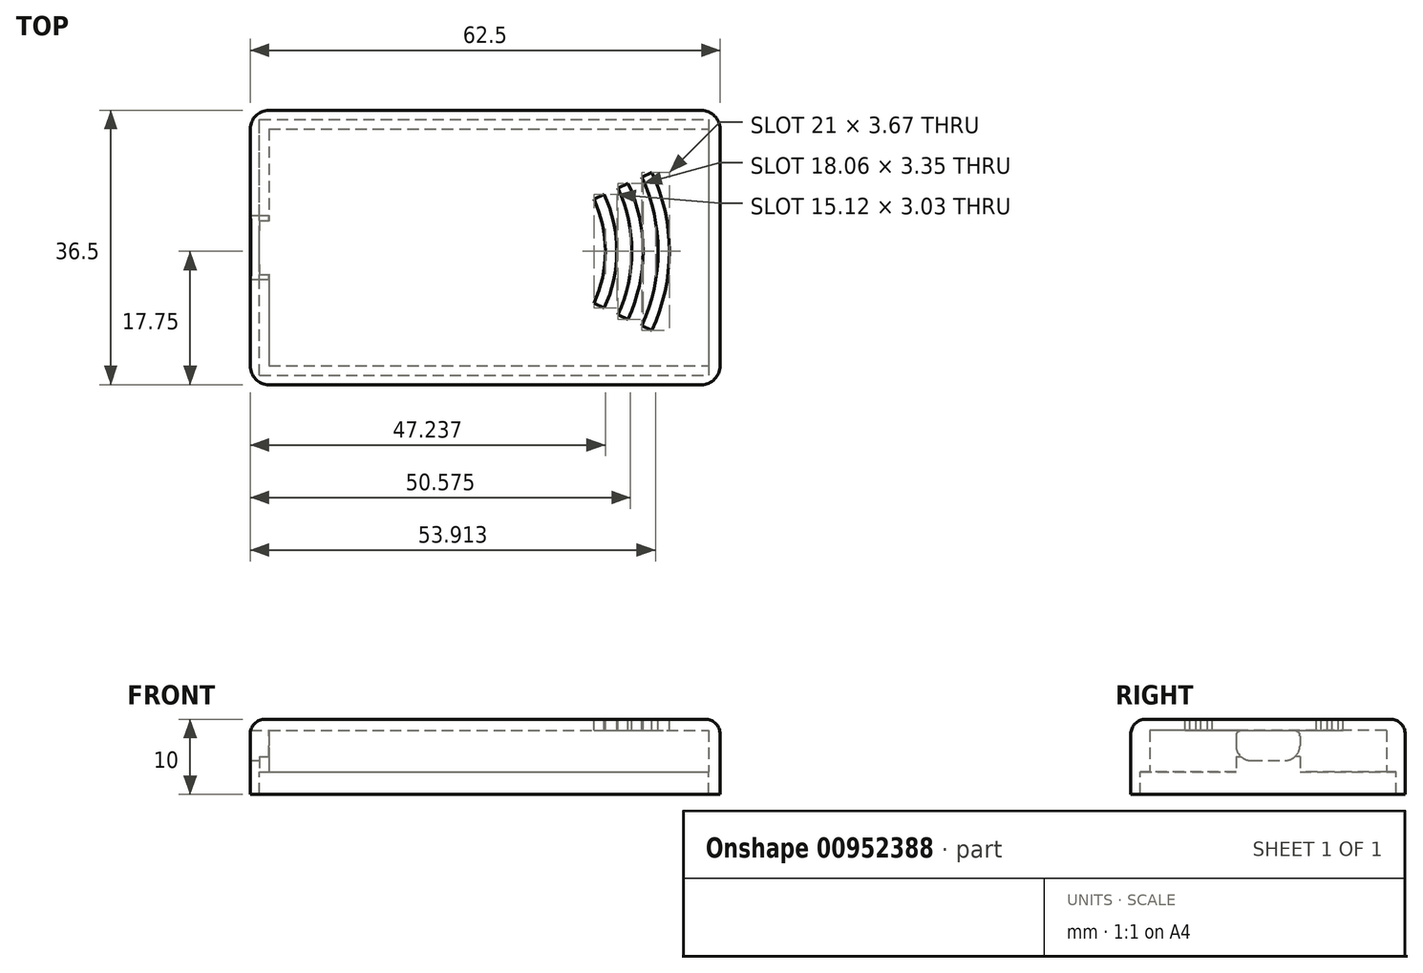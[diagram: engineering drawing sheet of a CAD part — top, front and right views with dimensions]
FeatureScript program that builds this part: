
annotation { "Feature Type Name" : "Feature", "Feature Type Description" : "" }
export const myFeature = defineFeature(function(context is Context, id is Id, definition is map)
    precondition{}
    {
        {
            var Q0;
            Q0=qCreatedBy(makeId("Top.planeOp"),FACE);
            var sketch = newSketch(context, id + "F0", { "sketchPlane" : qUnion([Q0])});
            skLineSegment(sketch, "E0.bottom", {"start": v(-30.75, 18.75) * mm, "end": v(31.75, 18.75) * mm});
            skLineSegment(sketch, "E0.top", {"start": v(-30.75, -17.75) * mm, "end": v(31.75, -17.75) * mm});
            skLineSegment(sketch, "E0.left", {"start": v(-30.75, 18.75) * mm, "end": v(-30.75, -17.75) * mm});
            skLineSegment(sketch, "E0.right", {"start": v(31.75, 18.75) * mm, "end": v(31.75, -17.75) * mm});
            skLineSegment(sketch, "E1.bottom", {"start": v(-28.25, 16.25) * mm, "end": v(30.25, 16.25) * mm});
            skLineSegment(sketch, "E1.top", {"start": v(-28.25, -15.25) * mm, "end": v(30.25, -15.25) * mm});
            skLineSegment(sketch, "E1.left", {"start": v(-28.25, 16.25) * mm, "end": v(-28.25, -15.25) * mm});
            skLineSegment(sketch, "E1.right", {"start": v(30.25, 16.25) * mm, "end": v(30.25, -15.25) * mm});
            skSolve(sketch);
        }
        {
            var Q0;
            Q0=makeQuery(id+"F0.imprint","IMPRINT",FACE,{"disambiguationData":[TD([[makeQuery(id+"F0.imprint","IMPRINT",EDGE,{"derivedFrom":sQuery(id+"F0.wireOp",EDGE,"E0.bottom")}),-1.0]])]});
            extrude(context, id + "F1", {"entities" : qUnion([Q0]), "offsetDistance" : 25 * mm, "depth" : 7 * mm});
        }
        {
            var Q0;
            Q0=makeQuery(id+"F1.opExtrude","CAP_FACE",FACE,{"disambiguationData":[OSD([sQuery(id+"F0.wireOp",EDGE,"E0.bottom"),sQuery(id+"F0.wireOp",EDGE,"E0.top"),sQuery(id+"F0.wireOp",EDGE,"E0.left"),sQuery(id+"F0.wireOp",EDGE,"E0.right"),sQuery(id+"F0.wireOp",EDGE,"E1.bottom"),sQuery(id+"F0.wireOp",EDGE,"E1.top"),sQuery(id+"F0.wireOp",EDGE,"E1.left"),sQuery(id+"F0.wireOp",EDGE,"E1.right")])],"isStart":false});
            var sketch = newSketch(context, id + "F2", { "sketchPlane" : qUnion([Q0])});
            skLineSegment(sketch, "E2.bottom", {"start": v(-28.25, 16.25) * mm, "end": v(30.25, 16.25) * mm});
            skLineSegment(sketch, "E2.top", {"start": v(-28.25, -15.25) * mm, "end": v(30.25, -15.25) * mm});
            skLineSegment(sketch, "E2.left", {"start": v(-28.25, 16.25) * mm, "end": v(-28.25, -15.25) * mm});
            skLineSegment(sketch, "E3", {"start": v(30.25, 16.25) * mm, "end": v(30.25, 7) * mm});
            skLineSegment(sketch, "E4", {"start": v(30.25, -6) * mm, "end": v(30.25, -15.25) * mm});
            skSolve(sketch);
        }
        {
            var Q0;
            Q0=makeQuery(id+"F2.imprint","IMPRINT",FACE,{"disambiguationData":[TD([[makeQuery(id+"F2.imprint","IMPRINT",EDGE,{"derivedFrom":sQuery(id+"F2.wireOp",EDGE,"E2.bottom")}),-1.0]])]});
            var Q1;
            Q1 = qSketchRegion(id + "F4", true);
            extrude(context, id + "F3", {"entities" : qUnion([Q0, Q1]), "operationType" : NewBodyOperationType.ADD, "oppositeDirection" : true, "offsetDistance" : 25 * mm, "depth" : 1.5 * mm});
        }
        {
            var Q0;
            Q0=makeQuery(id+"F1.opExtrude","CAP_FACE",FACE,{"disambiguationData":[OSD([sQuery(id+"F0.wireOp",EDGE,"E0.bottom"),sQuery(id+"F0.wireOp",EDGE,"E0.top"),sQuery(id+"F0.wireOp",EDGE,"E0.left"),sQuery(id+"F0.wireOp",EDGE,"E0.right"),sQuery(id+"F0.wireOp",EDGE,"E1.bottom"),sQuery(id+"F0.wireOp",EDGE,"E1.top"),sQuery(id+"F0.wireOp",EDGE,"E1.left"),sQuery(id+"F0.wireOp",EDGE,"E1.right")])],"isStart":true});
            var sketch = newSketch(context, id + "F4", { "sketchPlane" : qUnion([Q0])});
            skLineSegment(sketch, "E5.bottom", {"start": v(-30.75, 17.75) * mm, "end": v(31.75, 17.75) * mm});
            skLineSegment(sketch, "E5.top", {"start": v(-30.75, -18.75) * mm, "end": v(31.75, -18.75) * mm});
            skLineSegment(sketch, "E5.left", {"start": v(-30.75, 17.75) * mm, "end": v(-30.75, -18.75) * mm});
            skLineSegment(sketch, "E5.right", {"start": v(31.75, 17.75) * mm, "end": v(31.75, -18.75) * mm});
            skLineSegment(sketch, "E6.bottom", {"start": v(-29.5, 16.5) * mm, "end": v(30.25, 16.5) * mm});
            skLineSegment(sketch, "E6.top", {"start": v(-29.5, -17.52) * mm, "end": v(30.25, -17.52) * mm});
            skLineSegment(sketch, "E6.left", {"start": v(-29.5, 16.5) * mm, "end": v(-29.5, -17.52) * mm});
            skLineSegment(sketch, "E6.right", {"start": v(30.25, 16.5) * mm, "end": v(30.25, -17.52) * mm});
            skSolve(sketch);
        }
        {
            var Q0;
            Q0=makeQuery(id+"F4.imprint","IMPRINT",FACE,{"disambiguationData":[TD([[makeQuery(id+"F4.imprint","IMPRINT",EDGE,{"derivedFrom":sQuery(id+"F4.wireOp",EDGE,"E5.bottom")}),-1.0]])]});
            var Q1;
            {var subQ5=makeQuery(id+"F1.opExtrude","CAP_EDGE",EDGE,{"disambiguationData":[OSD([sQuery(id+"F0.wireOp",EDGE,"E1.right")])],"isStart":true});Q1=makeQuery(id+"F4.imprint","IMPRINT",FACE,{"disambiguationData":[TD([[makeQuery(id+"F4.imprint","IMPRINT",EDGE,{"derivedFrom":subQ5}),1.0]])]});}
            extrude(context, id + "F5", {"entities" : qUnion([Q0, Q1]), "operationType" : NewBodyOperationType.ADD, "offsetDistance" : 25 * mm, "depth" : 3 * mm});
        }
        {
            var Q0;
            Q0=makeQuery(id+"F1.opExtrude","SWEPT_FACE",FACE,{"disambiguationData":[OSD([sQuery(id+"F0.wireOp",EDGE,"E1.left")])]});
            var sketch = newSketch(context, id + "F6", { "sketchPlane" : qUnion([Q0])});
            skLineSegment(sketch, "E7.bottom", {"start": v(-3, 5.5) * mm, "end": v(4, 5.5) * mm});
            skLineSegment(sketch, "E7.top", {"start": v(-1.75, 1.5) * mm, "end": v(2.75, 1.5) * mm});
            skLineSegment(sketch, "E7.left", {"start": v(-3.75, 4.75) * mm, "end": v(-3.75, 3.5) * mm});
            skLineSegment(sketch, "E7.right", {"start": v(4.75, 4.75) * mm, "end": v(4.75, 3.5) * mm});
            skPoint(sketch, "E8.visualSharp", {"position": v(-3.75, 1.5) * mm});
            skArc(sketch, "E8.filletArc", {"start": v(-3.75, 3.5) * mm, "mid": v(-3.16, 2.09) * mm, "end": v(-1.75, 1.5) * mm});
            skPoint(sketch, "E9.visualSharp", {"position": v(4.75, 1.5) * mm});
            skArc(sketch, "E9.filletArc", {"start": v(2.75, 1.5) * mm, "mid": v(4.16, 2.09) * mm, "end": v(4.75, 3.5) * mm});
            skPoint(sketch, "E10.visualSharp", {"position": v(4.75, 5.5) * mm});
            skArc(sketch, "E10.filletArc", {"start": v(4.75, 4.75) * mm, "mid": v(4.53, 5.28) * mm, "end": v(4, 5.5) * mm});
            skPoint(sketch, "E11.visualSharp", {"position": v(-3.75, 5.5) * mm});
            skArc(sketch, "E11.filletArc", {"start": v(-3, 5.5) * mm, "mid": v(-3.53, 5.28) * mm, "end": v(-3.75, 4.75) * mm});
            skSolve(sketch);
        }
        {
            var Q0;
            Q0=makeQuery(id+"F6.imprint","IMPRINT",FACE,{"disambiguationData":[TD([[makeQuery(id+"F6.imprint","IMPRINT",EDGE,{"derivedFrom":sQuery(id+"F6.wireOp",EDGE,"E7.bottom")}),1.0]])]});
            extrude(context, id + "F7", {"entities" : qUnion([Q0]), "operationType" : NewBodyOperationType.REMOVE, "oppositeDirection" : true, "offsetDistance" : 25 * mm, "depth" : 2.5 * mm});
        }
        {
            var Q0;
            Q0=makeQuery(id+"F5.boolean.opBoolean","MERGE",EDGE,{"derivedFrom":[makeQuery(id+"F1.opExtrude","SWEPT_EDGE",EDGE,{"disambiguationData":[OSD([sQuery(id+"F0.wireOp",EDGE,"E0.bottom"),sQuery(id+"F0.wireOp",EDGE,"E0.left")])]}),makeQuery(id+"F5.opExtrude","SWEPT_EDGE",EDGE,{"disambiguationData":[OSD([sQuery(id+"F4.wireOp",EDGE,"E5.top"),sQuery(id+"F4.wireOp",EDGE,"E5.left")])]})]});
            var Q1;
            Q1=makeQuery(id+"F5.boolean.opBoolean","MERGE",EDGE,{"derivedFrom":[makeQuery(id+"F1.opExtrude","SWEPT_EDGE",EDGE,{"disambiguationData":[OSD([sQuery(id+"F0.wireOp",EDGE,"E0.top"),sQuery(id+"F0.wireOp",EDGE,"E0.left")])]}),makeQuery(id+"F5.opExtrude","SWEPT_EDGE",EDGE,{"disambiguationData":[OSD([sQuery(id+"F4.wireOp",EDGE,"E5.bottom"),sQuery(id+"F4.wireOp",EDGE,"E5.left")])]})]});
            var Q2;
            Q2=makeQuery(id+"F5.boolean.opBoolean","MERGE",EDGE,{"derivedFrom":[makeQuery(id+"F1.opExtrude","SWEPT_EDGE",EDGE,{"disambiguationData":[OSD([sQuery(id+"F0.wireOp",EDGE,"E0.bottom"),sQuery(id+"F0.wireOp",EDGE,"E0.right")])]}),makeQuery(id+"F5.opExtrude","SWEPT_EDGE",EDGE,{"disambiguationData":[OSD([sQuery(id+"F4.wireOp",EDGE,"E5.top"),sQuery(id+"F4.wireOp",EDGE,"E5.right")])]})]});
            var Q3;
            Q3=makeQuery(id+"F5.boolean.opBoolean","MERGE",EDGE,{"derivedFrom":[makeQuery(id+"F1.opExtrude","SWEPT_EDGE",EDGE,{"disambiguationData":[OSD([sQuery(id+"F0.wireOp",EDGE,"E0.top"),sQuery(id+"F0.wireOp",EDGE,"E0.right")])]}),makeQuery(id+"F5.opExtrude","SWEPT_EDGE",EDGE,{"disambiguationData":[OSD([sQuery(id+"F4.wireOp",EDGE,"E5.bottom"),sQuery(id+"F4.wireOp",EDGE,"E5.right")])]})]});
            fillet(context, id + "F8", {"entities" : qUnion([Q0, Q1, Q2, Q3]), "radius" : 2.5 * mm, "tangentPropagation" : true, "allowEdgeOverflow" : false});
        }
        {
            var Q0;
            Q0=makeQuery(id+"F1.opExtrude","CAP_EDGE",EDGE,{"disambiguationData":[OSD([sQuery(id+"F0.wireOp",EDGE,"E0.bottom")])],"isStart":false});
            fillet(context, id + "F9", {"entities" : qUnion([Q0]), "radius" : 2 * mm, "tangentPropagation" : true, "allowEdgeOverflow" : false});
        }
        {
            var Q0;
            Q0=makeQuery(id+"F1.opExtrude","CAP_FACE",FACE,{"disambiguationData":[OSD([sQuery(id+"F0.wireOp",EDGE,"E0.bottom"),sQuery(id+"F0.wireOp",EDGE,"E0.top"),sQuery(id+"F0.wireOp",EDGE,"E0.left"),sQuery(id+"F0.wireOp",EDGE,"E0.right"),sQuery(id+"F0.wireOp",EDGE,"E1.bottom"),sQuery(id+"F0.wireOp",EDGE,"E1.top"),sQuery(id+"F0.wireOp",EDGE,"E1.left"),sQuery(id+"F0.wireOp",EDGE,"E1.right")])],"isStart":true});
            var sketch = newSketch(context, id + "F10", { "sketchPlane" : qUnion([Q0])});
            skLineSegment(sketch, "E12.bottom", {"start": v(-29.5, 3.75) * mm, "end": v(-28.25, 3.75) * mm});
            skLineSegment(sketch, "E12.top", {"start": v(-29.5, -4.75) * mm, "end": v(-28.25, -4.75) * mm});
            skLineSegment(sketch, "E12.left", {"start": v(-29.5, 3.75) * mm, "end": v(-29.5, -4.75) * mm});
            skLineSegment(sketch, "E12.right", {"start": v(-28.25, 3.75) * mm, "end": v(-28.25, -4.75) * mm});
            skSolve(sketch);
        }
        {
            var Q0;
            Q0 = qSketchRegion(id + "F10", true);
            extrude(context, id + "F11", {"entities" : qUnion([Q0]), "operationType" : NewBodyOperationType.REMOVE, "oppositeDirection" : true, "offsetDistance" : 25 * mm, "depth" : 2 * mm});
        }
        {
            var Q0;
            {var subQ0=sQuery(id+"F0.wireOp",EDGE,"E1.right");Q0=makeQuery(id+"F3.boolean.opBoolean","MERGE",FACE,{"derivedFrom":[makeQuery(id+"F1.opExtrude","CAP_FACE",FACE,{"disambiguationData":[OSD([sQuery(id+"F0.wireOp",EDGE,"E0.bottom"),sQuery(id+"F0.wireOp",EDGE,"E0.top"),sQuery(id+"F0.wireOp",EDGE,"E0.left"),sQuery(id+"F0.wireOp",EDGE,"E0.right"),sQuery(id+"F0.wireOp",EDGE,"E1.bottom"),sQuery(id+"F0.wireOp",EDGE,"E1.top"),sQuery(id+"F0.wireOp",EDGE,"E1.left"),subQ0])],"isStart":false}),makeQuery(id+"F3.opExtrude","CAP_FACE",FACE,{"disambiguationData":[OSD([subQ0,sQuery(id+"F2.wireOp",EDGE,"E2.bottom"),sQuery(id+"F2.wireOp",EDGE,"E2.top"),sQuery(id+"F2.wireOp",EDGE,"E2.left"),sQuery(id+"F2.wireOp",EDGE,"E3"),sQuery(id+"F2.wireOp",EDGE,"E4")])],"isStart":true})]});}
            var sketch = newSketch(context, id + "F12", { "sketchPlane" : qUnion([Q0])});
            skArc(sketch, "E13", {"start": v(25, 0) * mm, "mid": v(24.41, 5.38) * mm, "end": v(22.69, 10.5) * mm});
            skArc(sketch, "E14", {"start": v(23.5, 0) * mm, "mid": v(22.95, 5.05) * mm, "end": v(21.33, 9.87) * mm});
            skArc(sketch, "E15", {"start": v(21.5, 0) * mm, "mid": v(21, 4.62) * mm, "end": v(19.51, 9.03) * mm});
            skArc(sketch, "E16", {"start": v(20, 0) * mm, "mid": v(19.53, 4.3) * mm, "end": v(18.15, 8.4) * mm});
            skArc(sketch, "E17", {"start": v(18, 0) * mm, "mid": v(17.58, 3.87) * mm, "end": v(16.33, 7.56) * mm});
            skArc(sketch, "E18", {"start": v(16.5, 0) * mm, "mid": v(16.11, 3.55) * mm, "end": v(14.97, 6.93) * mm});
            skArc(sketch, "E19.MirrorCS", {"start": v(25, 0) * mm, "mid": v(24.41, -5.38) * mm, "end": v(22.69, -10.5) * mm});
            skArc(sketch, "E20.MirrorCS", {"start": v(23.5, 0) * mm, "mid": v(22.95, -5.05) * mm, "end": v(21.33, -9.87) * mm});
            skArc(sketch, "E21.MirrorCS", {"start": v(21.5, 0) * mm, "mid": v(21, -4.62) * mm, "end": v(19.51, -9.03) * mm});
            skArc(sketch, "E22.MirrorCS", {"start": v(20, 0) * mm, "mid": v(19.53, -4.3) * mm, "end": v(18.15, -8.4) * mm});
            skArc(sketch, "E23.MirrorCS", {"start": v(18, 0) * mm, "mid": v(17.58, -3.87) * mm, "end": v(16.33, -7.56) * mm});
            skArc(sketch, "E24.MirrorCS", {"start": v(16.5, 0) * mm, "mid": v(16.11, -3.55) * mm, "end": v(14.97, -6.93) * mm});
            skPoint(sketch, "E25.orphan", {"position": v(0, 25) * mm});
            skPoint(sketch, "E26.orphan", {"position": v(0, 23.5) * mm});
            skPoint(sketch, "E27.orphan", {"position": v(0, 21.5) * mm});
            skPoint(sketch, "E28.orphan", {"position": v(0, 20) * mm});
            skPoint(sketch, "E29.orphan", {"position": v(0, 18) * mm});
            skPoint(sketch, "E30.orphan", {"position": v(0, 16.5) * mm});
            skPoint(sketch, "E31.orphan", {"position": v(0, -16.5) * mm});
            skPoint(sketch, "E32.orphan", {"position": v(0, -18) * mm});
            skPoint(sketch, "E33.orphan", {"position": v(0, -20) * mm});
            skPoint(sketch, "E34.orphan", {"position": v(0, -21.5) * mm});
            skPoint(sketch, "E35.orphan", {"position": v(0, -23.5) * mm});
            skPoint(sketch, "E36.orphan", {"position": v(0, -25) * mm});
            skPoint(sketch, "E37.orphan", {"position": v(9.2, -15) * mm});
            skPoint(sketch, "E38.orphan", {"position": v(9.2, 15) * mm});
            skLineSegment(sketch, "E39", {"start": v(14.97, -6.93) * mm, "end": v(16.33, -7.56) * mm});
            skPoint(sketch, "E39.endSnap0", {"position": v(18.76, -10.5) * mm});
            skLineSegment(sketch, "E40.MirrorCS", {"start": v(14.97, 6.93) * mm, "end": v(16.33, 7.56) * mm});
            skLineSegment(sketch, "E41.trimOffspring", {"start": v(21.33, 9.87) * mm, "end": v(22.69, 10.5) * mm});
            skLineSegment(sketch, "E42.trimOffspring", {"start": v(18.15, 8.4) * mm, "end": v(19.51, 9.03) * mm});
            skLineSegment(sketch, "E43.trimOffspring", {"start": v(18.15, -8.4) * mm, "end": v(19.51, -9.03) * mm});
            skLineSegment(sketch, "E44.trimOffspring", {"start": v(21.33, -9.87) * mm, "end": v(22.69, -10.5) * mm});
            skSolve(sketch);
        }
        {
            var Q0;
            Q0 = qSketchRegion(id + "F12", true);
            extrude(context, id + "F13", {"entities" : qUnion([Q0]), "operationType" : NewBodyOperationType.REMOVE, "oppositeDirection" : true, "depth" : 3 * mm, "offsetDistance" : 25 * mm});
        }
    });
